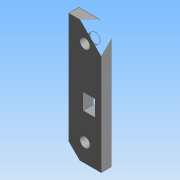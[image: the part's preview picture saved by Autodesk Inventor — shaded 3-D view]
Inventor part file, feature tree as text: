
AUTODESK INVENTOR PART (.ipt)
format: ipt  version: 2015 (Build 190159000, 159)  size: 92,672 bytes
history: native  units: mm
features: extrude x2, sketch x2
ambient origin geometry x8: Origin, YZ Plane, XZ Plane, XY Plane, X Axis, Y Axis, Z Axis, Center Point
bodies: Solid1 (feature_tree)
feature tree (4):
  extrude  "Extrusion1"  Depth=60.0mm
  extrude  "Extrusion2"  Depth=8.0mm
  sketch  "Sketch1"  dims[d0=5.0mm d1=0.0mm d2=60.0mm]
  sketch  "Sketch2"  dims[d3=16.0mm d4=8.0mm d5=5.0mm d6=9.0mm d7=8.0mm d8=9.0mm d9=5.0mm d10=8.0mm d11=5.0mm d13=26.0mm d14=10.0mm d15=0.0mm d16=5.5mm]
